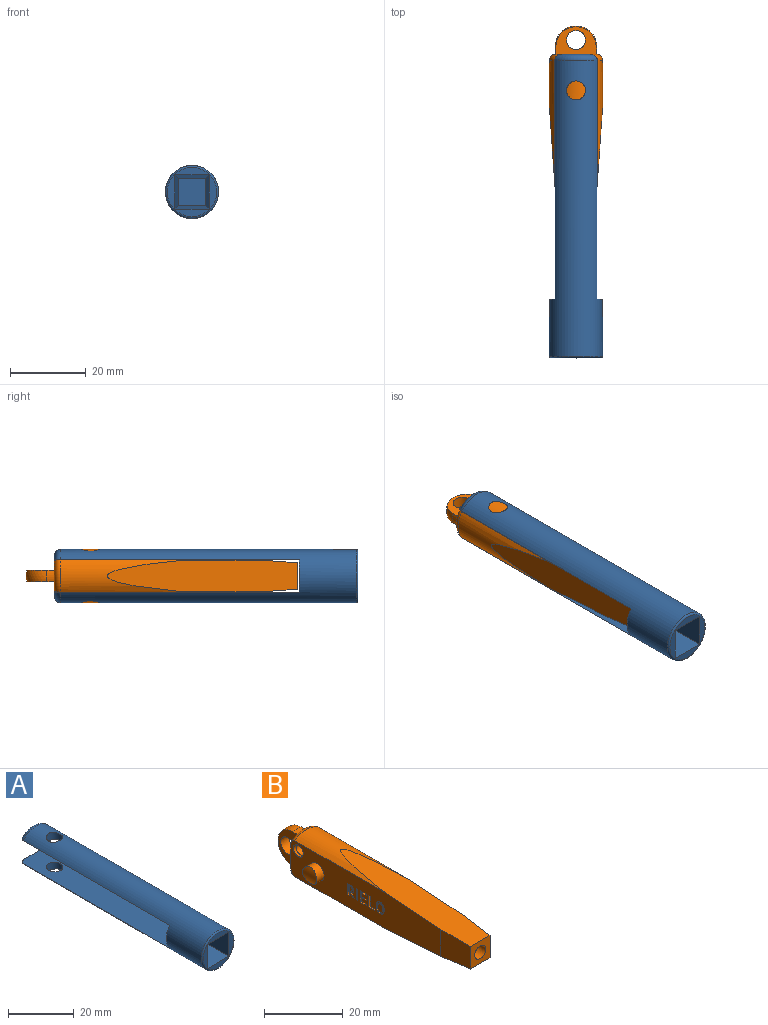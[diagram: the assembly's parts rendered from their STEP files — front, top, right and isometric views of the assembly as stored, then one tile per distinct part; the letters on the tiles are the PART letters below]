
ASSEMBLY  parts=2 mates=1
PART A: 20 faces, bbox 15.2x80x15.2 mm
  f0: cylinder r=7mm len=78mm, axis (0,-1,0), area 2223.8mm2, adj f9,f10,f11,f12,f13,f14,f15,f16
  f1: plane 6.86x1.2mm, normal (0,1,0), area 5.6mm2, adj f9,f16
  f2: plane 13x13mm, normal (0,-1,0), area 51.7mm2, adj f4,f5,f6,f7,f14
  f3: plane 6.86x1.2mm, normal (0,1,0), area 5.6mm2, adj f11,f15
  f4: plane 10x9mm, normal (0,-0.09,1), area 81.6mm2, adj f2,f5,f7,f8
  f5: plane 10x9mm, normal (-1,-0.09,0), area 81.6mm2, adj f2,f4,f6,f8
  f6: plane 10x9mm, normal (0,-0.09,-1), area 81.6mm2, adj f2,f5,f7,f8
  f7: plane 10x9mm, normal (1,-0.09,0), area 81.6mm2, adj f2,f4,f6,f8
  f8: plane 7.25x7.25mm, normal (0,-1,0), area 52.6mm2, adj f4,f5,f6,f7
  f9: plane 64.5x11.05mm, normal (0,0,-1), area 691.6mm2, adj f0,f1,f10,f13,f16
  f10: plane 14x8.6mm, normal (0,1,0), area 102.7mm2, adj f0,f9,f11,f19
  f11: plane 64.5x11.05mm, normal (0,0,1), area 691.6mm2, adj f0,f3,f10,f12,f15
  f12: cylinder r=2.5mm len=5mm, axis (0,0,1), area 38.8mm2, adj f0,f11
  f13: cylinder r=2.5mm len=5mm, axis (0,0,1), area 38.8mm2, adj f0,f9
  f14: torus R=6.5mm, axis (0,-1,0), area 33.6mm2, adj f0,f2
  f15: torus R=5.5mm, axis (0,-1,0), area 25.5mm2, adj f0,f3,f11
  f16: torus R=5.5mm, axis (0,-1,0), area 25.5mm2, adj f0,f1,f9
  f17: cone r=0mm half-angle=59deg, axis (0,1,0), area 8.2mm2, adj f18
  f18: cylinder r=1.5mm len=3.25mm, axis (0,1,0), area 30.6mm2, adj f17,f19
  f19: cone r=1.5mm half-angle=18.5deg, axis (0,1,0), area 8.1mm2, adj f10,f18
PART B: 245 faces, bbox 14x71.5x15.2 mm
  f0: plane 10.58x2.7mm, normal (0,1,0), area 24.9mm2, adj f2,f13,f14,f231
  f1: plane 53.99x11.2mm, normal (-1,0,0), area 528.8mm2, adj f3,f4,f5,f7,f8,f9,f11,f13
  f2: plane 53.99x11.2mm, normal (1,0,0), area 528.8mm2, adj f0,f3,f5,f6,f7,f9,f12,f13
  f3: cylinder r=7mm len=32.47mm, axis (0,-1,0), area 173.1mm2, adj f1,f2,f9,f13
  f4: plane 10.58x2.7mm, normal (0,1,0), area 24.9mm2, adj f1,f13,f14,f233
  f5: cylinder r=7mm len=32.47mm, axis (0,-1,0), area 173.1mm2, adj f1,f2,f7,f14
  f6: plane 10.01x8.4mm, normal (1,-0.07,0), area 77.3mm2, adj f2,f7,f9,f10
  f7: plane 50.05x8.4mm, normal (0,-0.07,1), area 360.7mm2, adj f1,f2,f5,f6,f8,f10
  f8: plane 10.01x8.4mm, normal (-1,-0.07,0), area 77.3mm2, adj f1,f7,f9,f10
  f9: plane 50.05x8.4mm, normal (0,-0.07,-1), area 360.7mm2, adj f1,f2,f3,f6,f8,f10
  f10: plane 7x7mm, normal (0,-1,0), area 36.4mm2, adj f6,f7,f8,f9,f244
  f11: cylinder r=2.5mm len=5mm, axis (-1,0,0), area 40.4mm2, adj f1,f230
  f12: cylinder r=2.5mm len=5mm, axis (-1,0,0), area 40.4mm2, adj f2,f229
  f13: torus R=5.5mm, axis (0,-1,0), area 21.6mm2, adj f0,f1,f2,f3,f4,f232
  f14: torus R=5.5mm, axis (0,-1,0), area 21.6mm2, adj f0,f1,f2,f4,f5,f234
  f15: plane 1.41x0.5mm, normal (0,0,-1), area 0.7mm2, adj f2,f16,f18,f19
  f16: plane 0.5x0.43mm, normal (0,1,0), area 0.2mm2, adj f2,f15,f17,f19
  f17: plane 1.41x0.5mm, normal (0,0,1), area 0.7mm2, adj f2,f16,f18,f19
  f18: plane 0.5x0.43mm, normal (0,-1,0), area 0.2mm2, adj f2,f15,f17,f19
  f19: plane 1.41x0.43mm, normal (1,0,0), area 0.6mm2, adj f15,f16,f17,f18
  f20: extruded ~0.55x0.5mm, area 0.3mm2, adj f2,f21,f39,f40
  f21: extruded ~0.75x0.5mm, area 0.4mm2, adj f2,f20,f22,f40
  f22: extruded ~0.5x0.02mm, area 0mm2, adj f2,f21,f23,f40
  f23: extruded ~0.73x0.5mm, area 0.4mm2, adj f2,f22,f24,f40
  f24: extruded ~0.55x0.5mm, area 0.3mm2, adj f2,f23,f25,f40
  f25: extruded ~0.5x0.43mm, area 0.3mm2, adj f2,f24,f26,f40
  f26: extruded ~0.54x0.5mm, area 0.3mm2, adj f2,f25,f27,f40
  f27: plane 0.5x0.47mm, normal (0,-1,0), area 0.2mm2, adj f2,f26,f28,f40
  f28: extruded ~0.5x0.3mm, area 0.2mm2, adj f2,f27,f29,f40
  f29: extruded ~0.5x0.25mm, area 0.2mm2, adj f2,f28,f30,f40
  f30: extruded ~0.5x0.4mm, area 0.2mm2, adj f2,f29,f31,f40
  f31: extruded ~0.56x0.5mm, area 0.3mm2, adj f2,f30,f32,f40
  f32: extruded ~0.5x0.02mm, area 0mm2, adj f2,f31,f33,f40
  f33: extruded ~0.57x0.5mm, area 0.3mm2, adj f2,f32,f34,f40
  f34: extruded ~0.5x0.4mm, area 0.2mm2, adj f2,f33,f35,f40
  f35: extruded ~0.5x0.25mm, area 0.2mm2, adj f2,f34,f36,f40
  f36: extruded ~0.5x0.3mm, area 0.2mm2, adj f2,f35,f37,f40
  f37: plane 0.5x0.47mm, normal (0,-1,0), area 0.2mm2, adj f2,f36,f38,f40
  f38: extruded ~0.54x0.5mm, area 0.3mm2, adj f2,f37,f39,f40
  f39: extruded ~0.5x0.43mm, area 0.3mm2, adj f2,f20,f38,f40
  f40: plane 3.57x1.36mm, normal (1,0,0), area 2.3mm2, adj f20,f21,f22,f23,f24,f25,f26,f27
  f41: plane 3.07x0.5mm, normal (0,-1,0), area 1.5mm2, adj f2,f42,f46,f47
  f42: plane 0.58x0.5mm, normal (0,0,-1), area 0.3mm2, adj f2,f41,f43,f47
  f43: plane 3.5x0.5mm, normal (0,1,0), area 1.7mm2, adj f2,f42,f44,f47
  f44: plane 2.19x0.5mm, normal (0,0,1), area 1.1mm2, adj f2,f43,f45,f47
  f45: plane 0.5x0.43mm, normal (0,-1,0), area 0.2mm2, adj f2,f44,f46,f47
  f46: plane 1.61x0.5mm, normal (0,0,-1), area 0.8mm2, adj f2,f41,f45,f47
  f47: plane 3.5x2.19mm, normal (1,0,0), area 2.7mm2, adj f41,f42,f43,f44,f45,f46
  f48: plane 0.5x0.39mm, normal (0,1,0), area 0.2mm2, adj f2,f49,f51,f52
  f49: plane 1.27x0.5mm, normal (0,0,1), area 0.6mm2, adj f2,f48,f50,f52
  f50: plane 0.5x0.39mm, normal (0,-1,0), area 0.2mm2, adj f2,f49,f51,f52
  f51: plane 1.27x0.5mm, normal (0,0,-1), area 0.6mm2, adj f2,f48,f50,f52
  f52: plane 1.27x0.39mm, normal (1,0,0), area 0.5mm2, adj f48,f49,f50,f51
  f53: plane 3.5x0.5mm, normal (0,-1,0), area 1.7mm2, adj f2,f54,f56,f57
  f54: plane 0.58x0.5mm, normal (0,0,-1), area 0.3mm2, adj f2,f53,f55,f57
  f55: plane 3.5x0.5mm, normal (0,1,0), area 1.7mm2, adj f2,f54,f56,f57
  f56: plane 0.58x0.5mm, normal (0,0,1), area 0.3mm2, adj f2,f53,f55,f57
  f57: plane 3.5x0.58mm, normal (1,0,0), area 2mm2, adj f53,f54,f55,f56
  f58: plane 0.5x0.43mm, normal (0,-1,0), area 0.2mm2, adj f2,f59,f61,f62
  f59: plane 1.41x0.5mm, normal (0,0,-1), area 0.7mm2, adj f2,f58,f60,f62
  f60: plane 0.5x0.43mm, normal (0,1,0), area 0.2mm2, adj f2,f59,f61,f62
  f61: plane 1.41x0.5mm, normal (0,0,1), area 0.7mm2, adj f2,f58,f60,f62
  f62: plane 1.41x0.43mm, normal (1,0,0), area 0.6mm2, adj f58,f59,f60,f61
  f63: plane 3.5x0.5mm, normal (0,-1,0), area 1.7mm2, adj f2,f64,f66,f67
  f64: plane 0.57x0.5mm, normal (0,0,-1), area 0.3mm2, adj f2,f63,f65,f67
  f65: plane 3.5x0.5mm, normal (0,1,0), area 1.7mm2, adj f2,f64,f66,f67
  f66: plane 0.57x0.5mm, normal (0,0,1), area 0.3mm2, adj f2,f63,f65,f67
  f67: plane 3.5x0.57mm, normal (1,0,0), area 2mm2, adj f63,f64,f65,f66
  f68: extruded ~0.5x0.03mm, area 0mm2, adj f2,f69,f94,f95
  f69: plane 1.27x0.66mm, normal (0,0.89,0.46), area 0.7mm2, adj f2,f68,f70,f95
  f70: plane 0.6x0.5mm, normal (0,0,1), area 0.3mm2, adj f2,f69,f71,f95
  f71: plane 1.38x0.8mm, normal (0,-0.87,-0.5), area 0.8mm2, adj f2,f70,f72,f95
  f72: extruded ~0.5x0.46mm, area 0.3mm2, adj f2,f71,f73,f95
  f73: extruded ~0.5x0.02mm, area 0mm2, adj f2,f72,f74,f95
  f74: extruded ~0.65x0.5mm, area 0.3mm2, adj f2,f73,f75,f95
  f75: extruded ~0.5x0.45mm, area 0.2mm2, adj f2,f74,f76,f95
  f76: extruded ~0.5x0.34mm, area 0.2mm2, adj f2,f75,f77,f95
  f77: extruded ~0.5x0.39mm, area 0.2mm2, adj f2,f76,f78,f95
  f78: extruded ~0.5x0.44mm, area 0.2mm2, adj f2,f77,f79,f95
  f79: plane 0.5x0.24mm, normal (0,0,-1), area 0.1mm2, adj f2,f78,f80,f95
  f80: plane 0.5x0.43mm, normal (0,1,0), area 0.2mm2, adj f2,f79,f81,f95
  f81: plane 0.5x0.23mm, normal (0,0,1), area 0.1mm2, adj f2,f80,f82,f95
  f82: extruded ~0.5x0.35mm, area 0.2mm2, adj f2,f81,f83,f95
  f83: extruded ~0.5x0.21mm, area 0.1mm2, adj f2,f82,f84,f95
  f84: extruded ~0.5x0.21mm, area 0.1mm2, adj f2,f83,f85,f95
  f85: extruded ~0.5x0.2mm, area 0.1mm2, adj f2,f84,f86,f95
  f86: extruded ~0.5x0.36mm, area 0.2mm2, adj f2,f85,f87,f95
  f87: extruded ~0.5x0.23mm, area 0.1mm2, adj f2,f86,f88,f95
  f88: extruded ~0.5x0.11mm, area 0.1mm2, adj f2,f87,f89,f95
  f89: extruded ~0.5x0.08mm, area 0mm2, adj f2,f88,f90,f95
  f90: extruded ~0.5x0.21mm, area 0.1mm2, adj f2,f89,f91,f95
  f91: plane 0.5x0.32mm, normal (0,0,-1), area 0.2mm2, adj f2,f90,f92,f95
  f92: plane 0.5x0.42mm, normal (0,1,0), area 0.2mm2, adj f2,f91,f93,f95
  f93: plane 0.5x0.27mm, normal (0,0,1), area 0.1mm2, adj f2,f92,f94,f95
  f94: extruded ~0.5x0.05mm, area 0mm2, adj f2,f68,f93,f95
  f95: plane 3.5x1.61mm, normal (1,0,0), area 2.4mm2, adj f68,f69,f70,f71,f72,f73,f74,f75
  f96: plane 3.5x0.5mm, normal (0,1,0), area 1.7mm2, adj f2,f97,f99,f100
  f97: plane 0.58x0.5mm, normal (0,0,1), area 0.3mm2, adj f2,f96,f98,f100
  f98: plane 3.5x0.5mm, normal (0,-1,0), area 1.7mm2, adj f2,f97,f99,f100
  f99: plane 0.58x0.5mm, normal (0,0,-1), area 0.3mm2, adj f2,f96,f98,f100
  f100: plane 3.5x0.58mm, normal (1,0,0), area 2mm2, adj f96,f97,f98,f99
  f101: extruded ~0.55x0.5mm, area 0.3mm2, adj f2,f102,f120,f121
  f102: extruded ~0.5x0.43mm, area 0.3mm2, adj f2,f101,f103,f121
  f103: extruded ~0.54x0.5mm, area 0.3mm2, adj f2,f102,f104,f121
  f104: plane 0.5x0.47mm, normal (0,1,0), area 0.2mm2, adj f2,f103,f105,f121
  f105: extruded ~0.5x0.3mm, area 0.2mm2, adj f2,f104,f106,f121
  f106: extruded ~0.5x0.25mm, area 0.2mm2, adj f2,f105,f107,f121
  f107: extruded ~0.5x0.4mm, area 0.2mm2, adj f2,f106,f108,f121
  f108: extruded ~0.58x0.5mm, area 0.3mm2, adj f2,f107,f109,f121
  f109: extruded ~0.5x0.02mm, area 0mm2, adj f2,f108,f110,f121
  f110: extruded ~0.56x0.5mm, area 0.3mm2, adj f2,f109,f111,f121
  f111: extruded ~0.5x0.4mm, area 0.2mm2, adj f2,f110,f112,f121
  f112: extruded ~0.5x0.25mm, area 0.2mm2, adj f2,f111,f113,f121
  f113: extruded ~0.5x0.3mm, area 0.2mm2, adj f2,f112,f114,f121
  f114: plane 0.5x0.47mm, normal (0,1,0), area 0.2mm2, adj f2,f113,f115,f121
  f115: extruded ~0.54x0.5mm, area 0.3mm2, adj f2,f114,f116,f121
  f116: extruded ~0.5x0.43mm, area 0.3mm2, adj f2,f115,f117,f121
  f117: extruded ~0.55x0.5mm, area 0.3mm2, adj f2,f116,f118,f121
  f118: extruded ~0.73x0.5mm, area 0.4mm2, adj f2,f117,f119,f121
  f119: extruded ~0.5x0.02mm, area 0mm2, adj f2,f118,f120,f121
  f120: extruded ~0.75x0.5mm, area 0.4mm2, adj f2,f101,f119,f121
  f121: plane 3.57x1.36mm, normal (1,0,0), area 2.2mm2, adj f101,f102,f103,f104,f105,f106,f107,f108
  f122: plane 1.41x0.5mm, normal (0,0,-1), area 0.7mm2, adj f1,f123,f125,f126
  f123: plane 0.5x0.43mm, normal (0,-1,0), area 0.2mm2, adj f1,f122,f124,f126
  f124: plane 1.41x0.5mm, normal (0,0,1), area 0.7mm2, adj f1,f123,f125,f126
  f125: plane 0.5x0.43mm, normal (0,1,0), area 0.2mm2, adj f1,f122,f124,f126
  f126: plane 1.41x0.43mm, normal (-1,0,0), area 0.6mm2, adj f122,f123,f124,f125
  f127: extruded ~0.55x0.5mm, area 0.3mm2, adj f1,f128,f146,f147
  f128: extruded ~0.75x0.5mm, area 0.4mm2, adj f1,f127,f129,f147
  f129: extruded ~0.5x0.02mm, area 0mm2, adj f1,f128,f130,f147
  f130: extruded ~0.73x0.5mm, area 0.4mm2, adj f1,f129,f131,f147
  f131: extruded ~0.55x0.5mm, area 0.3mm2, adj f1,f130,f132,f147
  f132: extruded ~0.5x0.43mm, area 0.3mm2, adj f1,f131,f133,f147
  f133: extruded ~0.54x0.5mm, area 0.3mm2, adj f1,f132,f134,f147
  f134: plane 0.5x0.47mm, normal (0,1,0), area 0.2mm2, adj f1,f133,f135,f147
  f135: extruded ~0.5x0.3mm, area 0.2mm2, adj f1,f134,f136,f147
  f136: extruded ~0.5x0.25mm, area 0.2mm2, adj f1,f135,f137,f147
  f137: extruded ~0.5x0.4mm, area 0.2mm2, adj f1,f136,f138,f147
  f138: extruded ~0.56x0.5mm, area 0.3mm2, adj f1,f137,f139,f147
  f139: extruded ~0.5x0.02mm, area 0mm2, adj f1,f138,f140,f147
  f140: extruded ~0.57x0.5mm, area 0.3mm2, adj f1,f139,f141,f147
  f141: extruded ~0.5x0.4mm, area 0.2mm2, adj f1,f140,f142,f147
  f142: extruded ~0.5x0.25mm, area 0.2mm2, adj f1,f141,f143,f147
  f143: extruded ~0.5x0.3mm, area 0.2mm2, adj f1,f142,f144,f147
  f144: plane 0.5x0.47mm, normal (0,1,0), area 0.2mm2, adj f1,f143,f145,f147
  f145: extruded ~0.54x0.5mm, area 0.3mm2, adj f1,f144,f146,f147
  f146: extruded ~0.5x0.43mm, area 0.3mm2, adj f1,f127,f145,f147
  f147: plane 3.57x1.36mm, normal (-1,0,0), area 2.3mm2, adj f127,f128,f129,f130,f131,f132,f133,f134
  f148: plane 3.07x0.5mm, normal (0,1,0), area 1.5mm2, adj f1,f149,f153,f154
  f149: plane 0.58x0.5mm, normal (0,0,-1), area 0.3mm2, adj f1,f148,f150,f154
  f150: plane 3.5x0.5mm, normal (0,-1,0), area 1.7mm2, adj f1,f149,f151,f154
  f151: plane 2.19x0.5mm, normal (0,0,1), area 1.1mm2, adj f1,f150,f152,f154
  f152: plane 0.5x0.43mm, normal (0,1,0), area 0.2mm2, adj f1,f151,f153,f154
  f153: plane 1.61x0.5mm, normal (0,0,-1), area 0.8mm2, adj f1,f148,f152,f154
  f154: plane 3.5x2.19mm, normal (-1,0,0), area 2.7mm2, adj f148,f149,f150,f151,f152,f153
  f155: plane 0.5x0.39mm, normal (0,-1,0), area 0.2mm2, adj f1,f156,f158,f159
  f156: plane 1.27x0.5mm, normal (0,0,1), area 0.6mm2, adj f1,f155,f157,f159
  f157: plane 0.5x0.39mm, normal (0,1,0), area 0.2mm2, adj f1,f156,f158,f159
  f158: plane 1.27x0.5mm, normal (0,0,-1), area 0.6mm2, adj f1,f155,f157,f159
  f159: plane 1.27x0.39mm, normal (-1,0,0), area 0.5mm2, adj f155,f156,f157,f158
  f160: plane 3.5x0.5mm, normal (0,1,0), area 1.7mm2, adj f1,f161,f163,f164
  f161: plane 0.58x0.5mm, normal (0,0,-1), area 0.3mm2, adj f1,f160,f162,f164
  f162: plane 3.5x0.5mm, normal (0,-1,0), area 1.7mm2, adj f1,f161,f163,f164
  f163: plane 0.58x0.5mm, normal (0,0,1), area 0.3mm2, adj f1,f160,f162,f164
  f164: plane 3.5x0.58mm, normal (-1,0,0), area 2mm2, adj f160,f161,f162,f163
  f165: plane 0.5x0.43mm, normal (0,1,0), area 0.2mm2, adj f1,f166,f168,f169
  f166: plane 1.41x0.5mm, normal (0,0,-1), area 0.7mm2, adj f1,f165,f167,f169
  f167: plane 0.5x0.43mm, normal (0,-1,0), area 0.2mm2, adj f1,f166,f168,f169
  f168: plane 1.41x0.5mm, normal (0,0,1), area 0.7mm2, adj f1,f165,f167,f169
  f169: plane 1.41x0.43mm, normal (-1,0,0), area 0.6mm2, adj f165,f166,f167,f168
  f170: plane 3.5x0.5mm, normal (0,1,0), area 1.7mm2, adj f1,f171,f173,f174
  f171: plane 0.57x0.5mm, normal (0,0,-1), area 0.3mm2, adj f1,f170,f172,f174
  f172: plane 3.5x0.5mm, normal (0,-1,0), area 1.7mm2, adj f1,f171,f173,f174
  f173: plane 0.57x0.5mm, normal (0,0,1), area 0.3mm2, adj f1,f170,f172,f174
  f174: plane 3.5x0.57mm, normal (-1,0,0), area 2mm2, adj f170,f171,f172,f173
  f175: extruded ~0.5x0.03mm, area 0mm2, adj f1,f176,f201,f202
  f176: plane 1.27x0.66mm, normal (0,-0.89,0.46), area 0.7mm2, adj f1,f175,f177,f202
  f177: plane 0.6x0.5mm, normal (0,0,1), area 0.3mm2, adj f1,f176,f178,f202
  f178: plane 1.38x0.8mm, normal (0,0.87,-0.5), area 0.8mm2, adj f1,f177,f179,f202
  f179: extruded ~0.5x0.46mm, area 0.3mm2, adj f1,f178,f180,f202
  f180: extruded ~0.5x0.02mm, area 0mm2, adj f1,f179,f181,f202
  f181: extruded ~0.65x0.5mm, area 0.3mm2, adj f1,f180,f182,f202
  f182: extruded ~0.5x0.45mm, area 0.2mm2, adj f1,f181,f183,f202
  f183: extruded ~0.5x0.34mm, area 0.2mm2, adj f1,f182,f184,f202
  f184: extruded ~0.5x0.39mm, area 0.2mm2, adj f1,f183,f185,f202
  f185: extruded ~0.5x0.44mm, area 0.2mm2, adj f1,f184,f186,f202
  f186: plane 0.5x0.24mm, normal (0,0,-1), area 0.1mm2, adj f1,f185,f187,f202
  f187: plane 0.5x0.43mm, normal (0,-1,0), area 0.2mm2, adj f1,f186,f188,f202
  f188: plane 0.5x0.23mm, normal (0,0,1), area 0.1mm2, adj f1,f187,f189,f202
  f189: extruded ~0.5x0.35mm, area 0.2mm2, adj f1,f188,f190,f202
  f190: extruded ~0.5x0.21mm, area 0.1mm2, adj f1,f189,f191,f202
  f191: extruded ~0.5x0.21mm, area 0.1mm2, adj f1,f190,f192,f202
  f192: extruded ~0.5x0.2mm, area 0.1mm2, adj f1,f191,f193,f202
  f193: extruded ~0.5x0.36mm, area 0.2mm2, adj f1,f192,f194,f202
  f194: extruded ~0.5x0.23mm, area 0.1mm2, adj f1,f193,f195,f202
  f195: extruded ~0.5x0.11mm, area 0.1mm2, adj f1,f194,f196,f202
  f196: extruded ~0.5x0.08mm, area 0mm2, adj f1,f195,f197,f202
  f197: extruded ~0.5x0.21mm, area 0.1mm2, adj f1,f196,f198,f202
  f198: plane 0.5x0.32mm, normal (0,0,-1), area 0.2mm2, adj f1,f197,f199,f202
  f199: plane 0.5x0.42mm, normal (0,-1,0), area 0.2mm2, adj f1,f198,f200,f202
  f200: plane 0.5x0.27mm, normal (0,0,1), area 0.1mm2, adj f1,f199,f201,f202
  f201: extruded ~0.5x0.05mm, area 0mm2, adj f1,f175,f200,f202
  f202: plane 3.5x1.61mm, normal (-1,0,0), area 2.4mm2, adj f175,f176,f177,f178,f179,f180,f181,f182
  f203: plane 3.5x0.5mm, normal (0,-1,0), area 1.7mm2, adj f1,f204,f206,f207
  f204: plane 0.58x0.5mm, normal (0,0,1), area 0.3mm2, adj f1,f203,f205,f207
  f205: plane 3.5x0.5mm, normal (0,1,0), area 1.7mm2, adj f1,f204,f206,f207
  f206: plane 0.58x0.5mm, normal (0,0,-1), area 0.3mm2, adj f1,f203,f205,f207
  f207: plane 3.5x0.58mm, normal (-1,0,0), area 2mm2, adj f203,f204,f205,f206
  f208: extruded ~0.55x0.5mm, area 0.3mm2, adj f1,f209,f227,f228
  f209: extruded ~0.5x0.43mm, area 0.3mm2, adj f1,f208,f210,f228
  f210: extruded ~0.54x0.5mm, area 0.3mm2, adj f1,f209,f211,f228
  f211: plane 0.5x0.47mm, normal (0,-1,0), area 0.2mm2, adj f1,f210,f212,f228
  f212: extruded ~0.5x0.3mm, area 0.2mm2, adj f1,f211,f213,f228
  f213: extruded ~0.5x0.25mm, area 0.2mm2, adj f1,f212,f214,f228
  f214: extruded ~0.5x0.4mm, area 0.2mm2, adj f1,f213,f215,f228
  f215: extruded ~0.58x0.5mm, area 0.3mm2, adj f1,f214,f216,f228
  f216: extruded ~0.5x0.02mm, area 0mm2, adj f1,f215,f217,f228
  f217: extruded ~0.56x0.5mm, area 0.3mm2, adj f1,f216,f218,f228
  f218: extruded ~0.5x0.4mm, area 0.2mm2, adj f1,f217,f219,f228
  f219: extruded ~0.5x0.25mm, area 0.2mm2, adj f1,f218,f220,f228
  f220: extruded ~0.5x0.3mm, area 0.2mm2, adj f1,f219,f221,f228
  f221: plane 0.5x0.47mm, normal (0,-1,0), area 0.2mm2, adj f1,f220,f222,f228
  f222: extruded ~0.54x0.5mm, area 0.3mm2, adj f1,f221,f223,f228
  f223: extruded ~0.5x0.43mm, area 0.3mm2, adj f1,f222,f224,f228
  f224: extruded ~0.55x0.5mm, area 0.3mm2, adj f1,f223,f225,f228
  f225: extruded ~0.73x0.5mm, area 0.4mm2, adj f1,f224,f226,f228
  f226: extruded ~0.5x0.02mm, area 0mm2, adj f1,f225,f227,f228
  f227: extruded ~0.75x0.5mm, area 0.4mm2, adj f1,f208,f226,f228
  f228: plane 3.57x1.36mm, normal (-1,0,0), area 2.2mm2, adj f208,f209,f210,f211,f212,f213,f214,f215
  f229: cylinder r=7mm len=5mm, axis (0,1,0), area 20mm2, adj f12
  f230: cylinder r=7mm len=5mm, axis (0,1,0), area 20mm2, adj f11
  f231: plane 10.58x7.29mm, normal (1,0,0), area 45.5mm2, adj f0,f232,f234,f235,f236
  f232: cylinder r=5.5mm len=3mm, axis (0,-1,0), area 6.1mm2, adj f13,f231,f233,f235
  f233: plane 10.58x7.29mm, normal (-1,0,0), area 45.5mm2, adj f4,f232,f234,f235,f236
  f234: cylinder r=5.5mm len=3mm, axis (0,-1,0), area 6.1mm2, adj f14,f231,f233,f235
  f235: sphere r=5.5mm, area 51.8mm2, adj f231,f232,f233,f234
  f236: cylinder r=2.5mm len=5mm, axis (-1,0,0), area 47.1mm2, adj f231,f233
  f237: cone r=0mm half-angle=59deg, axis (1,0,0), area 8.2mm2, adj f238
  f238: cylinder r=1.5mm len=3.25mm, axis (1,0,0), area 30.6mm2, adj f237,f239
  f239: cone r=1.5mm half-angle=18.5deg, axis (1,0,0), area 8.1mm2, adj f2,f238
  f240: cone r=0mm half-angle=59deg, axis (-1,0,0), area 8.2mm2, adj f241
  f241: cylinder r=1.5mm len=3.25mm, axis (-1,0,0), area 30.6mm2, adj f240,f242
  f242: cone r=1.5mm half-angle=18.5deg, axis (-1,0,0), area 8.1mm2, adj f1,f241
  f243: cone r=0mm half-angle=59deg, axis (0,-1,0), area 14.7mm2, adj f244
  f244: cylinder r=2mm len=5mm, axis (0,-1,0), area 62.8mm2, adj f10,f243
PLACE A t=(0,-3,0)mm
PLACE B rot(axis=(0,-1,0),90deg) t=(0,13,0)mm
MATE revolute B.f11 <-> A.f12  axis (0,0,-1) through (0,67.5,-4.2)mm
